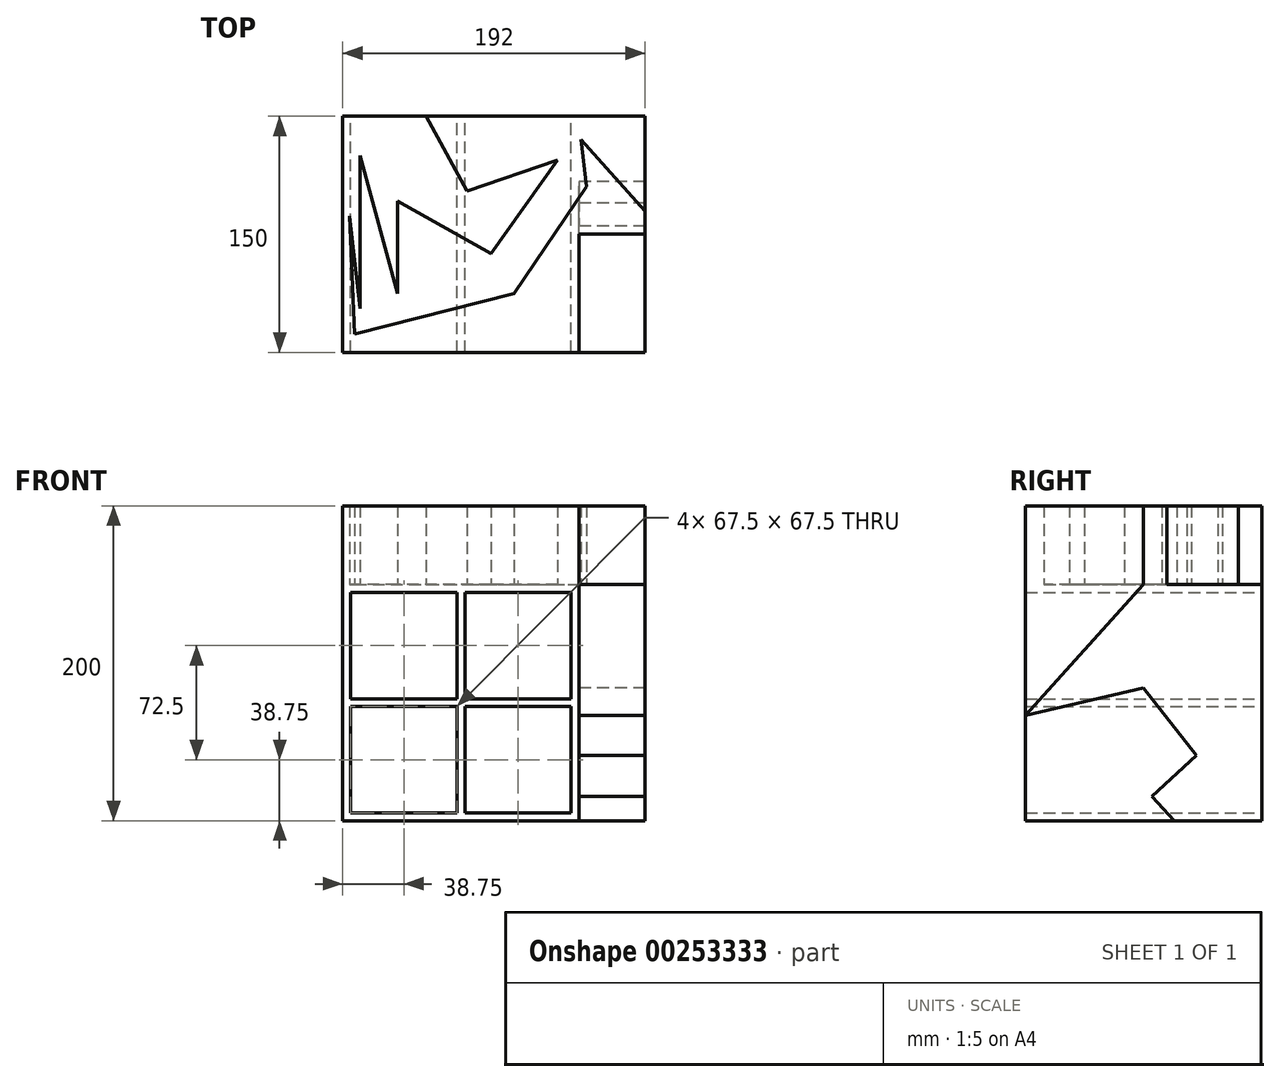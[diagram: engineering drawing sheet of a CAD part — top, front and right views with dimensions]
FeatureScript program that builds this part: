
annotation { "Feature Type Name" : "Feature", "Feature Type Description" : "" }
export const myFeature = defineFeature(function(context is Context, id is Id, definition is map)
    precondition{}
    {
        {
            var Q0;
            Q0=qCreatedBy(makeId("Front.planeOp"),FACE);
            var sketch = newSketch(context, id + "F0", { "sketchPlane" : qUnion([Q0])});
            skLineSegment(sketch, "E0.bottom", {"start": v(0, 0) * mm, "end": v(150, 0) * mm});
            skLineSegment(sketch, "E0.top", {"start": v(0, 150) * mm, "end": v(150, 150) * mm});
            skLineSegment(sketch, "E0.left", {"start": v(0, 0) * mm, "end": v(0, 150) * mm});
            skLineSegment(sketch, "E0.right", {"start": v(150, 0) * mm, "end": v(150, 150) * mm});
            skLineSegment(sketch, "E1.0", {"start": v(5, 145) * mm, "end": v(72.5, 145) * mm});
            skLineSegment(sketch, "E2.0", {"start": v(5, 5) * mm, "end": v(5, 72.5) * mm});
            skLineSegment(sketch, "E3.0", {"start": v(145, 5) * mm, "end": v(145, 72.5) * mm});
            skLineSegment(sketch, "E4.0", {"start": v(5, 5) * mm, "end": v(72.5, 5) * mm});
            skLineSegment(sketch, "E5.0", {"start": v(72.5, 5) * mm, "end": v(72.5, 72.5) * mm});
            skLineSegment(sketch, "E6.0", {"start": v(77.5, 5) * mm, "end": v(77.5, 72.5) * mm});
            skLineSegment(sketch, "E7.0", {"start": v(5, 77.5) * mm, "end": v(72.5, 77.5) * mm});
            skLineSegment(sketch, "E8.0", {"start": v(5, 72.5) * mm, "end": v(72.5, 72.5) * mm});
            skLineSegment(sketch, "E9.trimOffspring", {"start": v(77.5, 77.5) * mm, "end": v(145, 77.5) * mm});
            skLineSegment(sketch, "E10.trimOffspring", {"start": v(77.5, 72.5) * mm, "end": v(145, 72.5) * mm});
            skLineSegment(sketch, "E11.trimOffspring", {"start": v(77.5, 77.5) * mm, "end": v(77.5, 145) * mm});
            skLineSegment(sketch, "E12.trimOffspring", {"start": v(72.5, 77.5) * mm, "end": v(72.5, 145) * mm});
            skLineSegment(sketch, "E13.trimOffspring", {"start": v(5, 77.5) * mm, "end": v(5, 145) * mm});
            skLineSegment(sketch, "E14.trimOffspring", {"start": v(145, 77.5) * mm, "end": v(145, 145) * mm});
            skLineSegment(sketch, "E15.trimOffspring", {"start": v(77.5, 5) * mm, "end": v(145, 5) * mm});
            skLineSegment(sketch, "E16.trimOffspring", {"start": v(77.5, 145) * mm, "end": v(145, 145) * mm});
            skSolve(sketch);
        }
        {
            var Q0;
            Q0=makeQuery(id+"F0.imprint","IMPRINT",FACE,{"disambiguationData":[TD([[makeQuery(id+"F0.imprint","IMPRINT",EDGE,{"derivedFrom":sQuery(id+"F0.wireOp",EDGE,"E0.bottom")}),1.0]])]});
            extrude(context, id + "F1", {"entities" : qUnion([Q0]), "depth" : 150 * mm});
        }
        {
            var Q0;
            Q0=makeQuery(id+"F1.opExtrude","SWEPT_FACE",FACE,{"disambiguationData":[OSD([sQuery(id+"F0.wireOp",EDGE,"E0.right")])]});
            var sketch = newSketch(context, id + "F2", { "sketchPlane" : qUnion([Q0])});
            skLineSegment(sketch, "E17", {"start": v(-75, 150) * mm, "end": v(-150, 66.95) * mm});
            skLineSegment(sketch, "E18", {"start": v(-150, 66.95) * mm, "end": v(-75.04, 84.21) * mm});
            skLineSegment(sketch, "E19", {"start": v(-75.04, 84.21) * mm, "end": v(-41.6, 41.5) * mm});
            skLineSegment(sketch, "E20", {"start": v(-41.6, 41.5) * mm, "end": v(-69.65, 15.39) * mm});
            skLineSegment(sketch, "E21", {"start": v(-69.65, 15.39) * mm, "end": v(-55.33, 0) * mm});
            skSolve(sketch);
        }
        {
            var Q0;
            Q0 = qSketchRegion(id + "F2", true);
            var Q1;
            {var subQ0=sQuery(id+"F2.wireOp",EDGE,"E17");Q1=makeQuery(id+"F2.imprint","IMPRINT",FACE,{"disambiguationData":[TD([[makeQuery(id+"F2.imprint","IMPRINT",EDGE,{"derivedFrom":subQ0}),1.0]])]});}
            extrude(context, id + "F3", {"entities" : qUnion([Q0, Q1]), "operationType" : NewBodyOperationType.ADD, "depth" : 42 * mm});
        }
        {
            var Q0;
            {var subQ0=sQuery(id+"F0.wireOp",EDGE,"E0.top");Q0=makeQuery(id+"F3.boolean.opBoolean","MERGE",FACE,{"derivedFrom":[makeQuery(id+"F1.opExtrude","SWEPT_FACE",FACE,{"disambiguationData":[OSD([subQ0])]}),makeQuery(id+"F3.opExtrude","SWEPT_FACE",FACE,{"disambiguationData":[OSD([subQ0,sQuery(id+"F0.wireOp",EDGE,"E0.right")])]})]});}
            var sketch = newSketch(context, id + "F4", { "sketchPlane" : qUnion([Q0])});
            skLineSegment(sketch, "E22", {"start": v(52.73, 0) * mm, "end": v(78.89, -47.46) * mm});
            skLineSegment(sketch, "E23", {"start": v(78.89, -47.46) * mm, "end": v(136.45, -27.83) * mm});
            skLineSegment(sketch, "E24", {"start": v(136.45, -27.83) * mm, "end": v(94.18, -87.26) * mm});
            skLineSegment(sketch, "E25", {"start": v(94.18, -87.26) * mm, "end": v(34.62, -53.78) * mm});
            skLineSegment(sketch, "E26", {"start": v(34.62, -53.78) * mm, "end": v(34.62, -112.55) * mm});
            skLineSegment(sketch, "E27", {"start": v(34.62, -112.55) * mm, "end": v(11.04, -24.98) * mm});
            skLineSegment(sketch, "E28", {"start": v(11.04, -24.98) * mm, "end": v(11.04, -122.2) * mm});
            skLineSegment(sketch, "E29", {"start": v(11.04, -122.2) * mm, "end": v(4.16, -63.47) * mm});
            skLineSegment(sketch, "E30", {"start": v(4.16, -63.47) * mm, "end": v(7.6, -138.3) * mm});
            skPoint(sketch, "E30.endSnap0", {"position": v(7.6, -92.84) * mm});
            skLineSegment(sketch, "E31", {"start": v(7.6, -138.3) * mm, "end": v(108.6, -112.55) * mm});
            skLineSegment(sketch, "E32", {"start": v(108.6, -112.55) * mm, "end": v(154.84, -44.66) * mm});
            skLineSegment(sketch, "E33", {"start": v(154.84, -44.66) * mm, "end": v(151.34, -14.71) * mm});
            skLineSegment(sketch, "E34", {"start": v(151.34, -14.71) * mm, "end": v(192, -60.3) * mm});
            skSolve(sketch);
        }
        {
            var Q0;
            Q0 = qSketchRegion(id + "F4", true);
            var Q1;
            {var subQ5=sQuery(id+"F4.wireOp",EDGE,"E22");Q1=makeQuery(id+"F4.imprint","IMPRINT",FACE,{"disambiguationData":[TD([[makeQuery(id+"F4.imprint","IMPRINT",EDGE,{"derivedFrom":subQ5}),-1.0]])]});}
            extrude(context, id + "F5", {"entities" : qUnion([Q0, Q1]), "operationType" : NewBodyOperationType.ADD, "depth" : 50 * mm});
        }
    });
